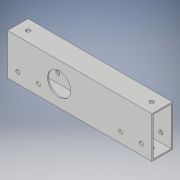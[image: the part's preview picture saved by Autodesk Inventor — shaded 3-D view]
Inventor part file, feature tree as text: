
AUTODESK INVENTOR PART (.ipt)
format: ipt  version: 2018 (Build 220112000, 112)  size: 130,560 bytes
history: native  units: in
note: dims shown in document units (in); Inventor stores cm internally (conversion verified against a paired STEP export)
features: hole x7, sketch x2, extrude x1, shell x1
ambient origin geometry x8: Origin, YZ Plane, XZ Plane, XY Plane, X Axis, Y Axis, Z Axis, Center Point
bodies: Solid1 (feature_tree)
feature tree (11):
  extrude  "Extrusion1"  Depth=2.0in
  shell  "Shell1"  Thickness=1.0in
  hole  "Hole1"  [1 undecoded]
  hole  "Hole2"  [1 undecoded]
  hole  "Hole3"  [1 undecoded]
  hole  "Hole4"  [1 undecoded]
  hole  "Hole5"  [1 undecoded]
  hole  "Hole6"  [1 undecoded]
  hole  "Hole7"  [1 undecoded]
  sketch  "Sketch1"  dims[d0=7.0in d1=2.0in d2=1.0in d3=0.0in]
  sketch  "Sketch2"  dims[d4=0.0625in d5=2.5in d6=1.125in d7=0.75in d8=0.375in d9=0.25in d10=0.5635in d11=1.0in d12=0.8108in d13=1.0in d14=0.5in d15=0.5in d16=0.2031in d17=0.75in d18=0.375in d19=0.25in d20=0.5635in d21=1.0in d22=0.8108in d23=1.5in d24=0.5in d25=0.2031in d26=0.75in d27=0.375in d28=0.25in d29=0.5635in d30=1.0in d31=0.8108in d32=0.5in d33=0.5in d34=0.2031in d35=0.75in d36=0.375in d37=0.25in d38=0.5635in d39=1.0in d40=0.8108in d41=1.5in d42=0.5in d43=0.2031in d44=0.75in d45=0.375in d46=0.25in d47=0.5635in d48=1.0in d49=0.8108in d50=0.5in d51=0.5in d52=0.2031in d53=0.75in d54=0.375in d55=0.25in d56=0.5635in d57=1.0in d58=0.8108in d59=0.5in d60=0.5in d61=0.2031in d62=0.75in d63=0.375in d64=0.25in d65=0.5635in d66=1.0in d67=0.8108in]
note: 7 required parameter values undecoded (feature->parameter linkage not recoverable at this tier; creation-order binding heuristic only, values carry confidence <= 0.55)
